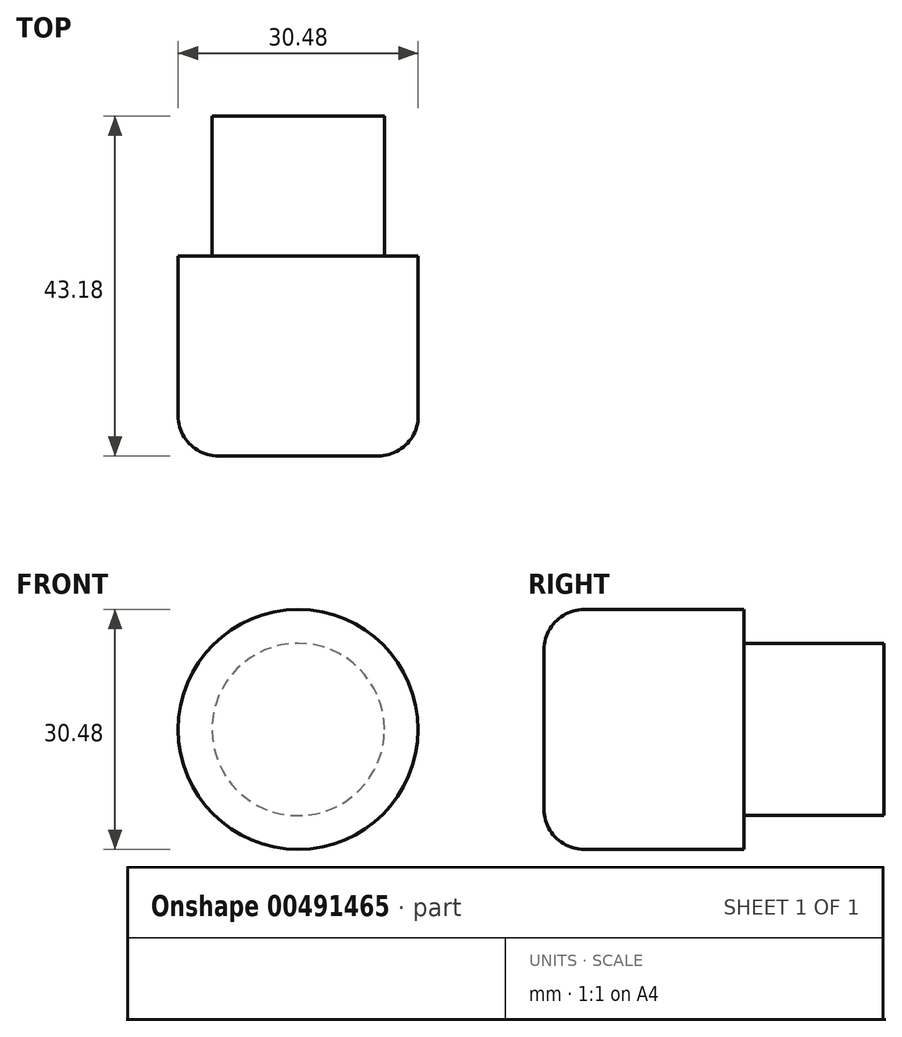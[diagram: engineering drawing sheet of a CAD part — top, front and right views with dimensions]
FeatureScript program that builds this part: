
annotation { "Feature Type Name" : "Feature", "Feature Type Description" : "" }
export const myFeature = defineFeature(function(context is Context, id is Id, definition is map)
    precondition{}
    {
        {
            var Q0;
            Q0=qCreatedBy(makeId("Front.planeOp"),FACE);
            var sketch = newSketch(context, id + "F0", { "sketchPlane" : qUnion([Q0])});
            skCircle(sketch, "E0", {"center": v(0, 0) * mm, "radius": 10.95 * mm});
            skSolve(sketch);
        }
        {
            var Q0;
            Q0=makeQuery(id+"F0.imprint","IMPRINT",FACE,{"disambiguationData":[TD([[makeQuery(id+"F0.imprint","IMPRINT",EDGE,{"derivedFrom":sQuery(id+"F0.wireOp",EDGE,"E0")}),1.0]])]});
            extrude(context, id + "F1", {"entities" : qUnion([Q0]), "depth" : 17.78 * mm});
        }
        {
            var Q0;
            Q0=makeQuery(id+"F1.opExtrude","CAP_FACE",FACE,{"disambiguationData":[OSD([sQuery(id+"F0.wireOp",EDGE,"E0")])],"isStart":false});
            var sketch = newSketch(context, id + "F2", { "sketchPlane" : qUnion([Q0])});
            skCircle(sketch, "E1", {"center": v(0, 0) * mm, "radius": 15.24 * mm});
            skSolve(sketch);
        }
        {
            var Q0;
            Q0=makeQuery(id+"F2.imprint","IMPRINT",FACE,{"disambiguationData":[TD([[makeQuery(id+"F2.imprint","IMPRINT",EDGE,{"derivedFrom":sQuery(id+"F2.wireOp",EDGE,"E1")}),1.0]])]});
            var Q1;
            Q1=makeQuery(id+"F2.imprint","IMPRINT",FACE,{"disambiguationData":[TD([[makeQuery(id+"F2.imprint","IMPRINT",EDGE,{"derivedFrom":makeQuery(id+"F1.opExtrude","CAP_EDGE",EDGE,{"disambiguationData":[OSD([sQuery(id+"F0.wireOp",EDGE,"E0")])],"isStart":false})}),1.0]])]});
            extrude(context, id + "F3", {"entities" : qUnion([Q0, Q1]), "operationType" : NewBodyOperationType.ADD, "depth" : 25.4 * mm});
        }
        {
            var Q0;
            Q0=makeQuery(id+"F3.opExtrude","CAP_EDGE",EDGE,{"disambiguationData":[OSD([sQuery(id+"F2.wireOp",EDGE,"E1")])],"isStart":false});
            fillet(context, id + "F4", {"entities" : qUnion([Q0]), "radius" : 5.08 * mm, "tangentPropagation" : true, "allowEdgeOverflow" : false});
        }
    });
